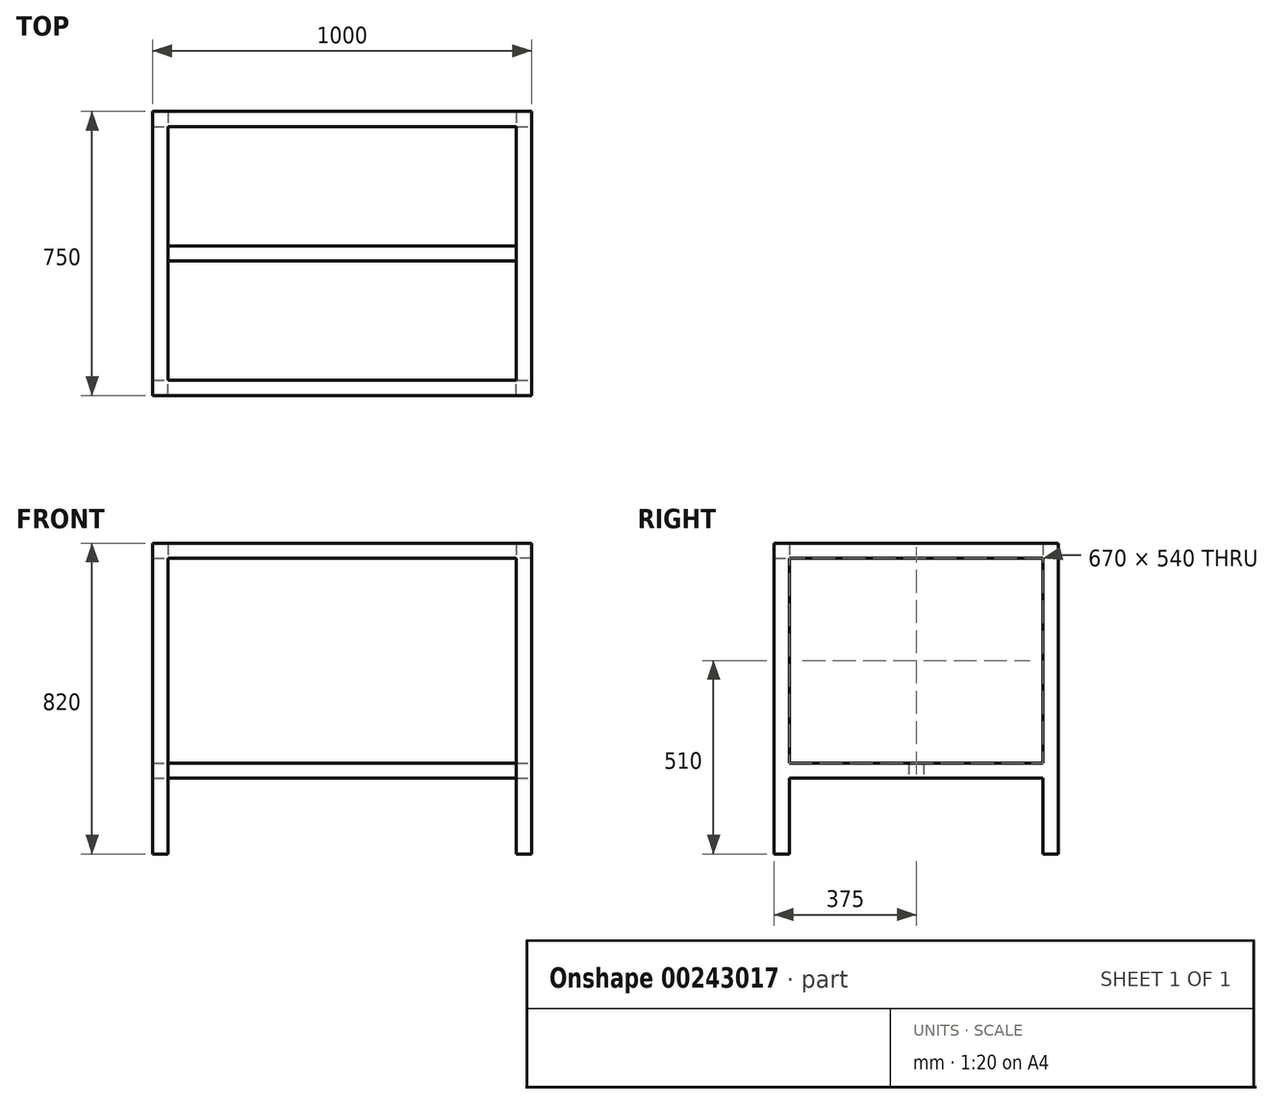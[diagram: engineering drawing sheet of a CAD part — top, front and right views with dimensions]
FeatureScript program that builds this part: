
annotation { "Feature Type Name" : "Feature", "Feature Type Description" : "" }
export const myFeature = defineFeature(function(context is Context, id is Id, definition is map)
    precondition{}
    {
        {
            var Q0;
            Q0=qCreatedBy(makeId("Top.planeOp"),FACE);
            var sketch = newSketch(context, id + "F0", { "sketchPlane" : qUnion([Q0])});
            skLineSegment(sketch, "E0.bottom", {"start": v(500, 375) * mm, "end": v(-500, 375) * mm});
            skLineSegment(sketch, "E0.top", {"start": v(500, -375) * mm, "end": v(-500, -375) * mm});
            skLineSegment(sketch, "E0.left", {"start": v(500, 375) * mm, "end": v(500, -375) * mm});
            skLineSegment(sketch, "E0.right", {"start": v(-500, 375) * mm, "end": v(-500, -375) * mm});
            skPoint(sketch, "E0.middle", {"position": v(0, 0) * mm});
            skLineSegment(sketch, "E1.bottom", {"start": v(460, 335) * mm, "end": v(0, 335) * mm});
            skLineSegment(sketch, "E1.top", {"start": v(460, -335) * mm, "end": v(0, -335) * mm});
            skLineSegment(sketch, "E1.left", {"start": v(460, 335) * mm, "end": v(460, -335) * mm});
            skLineSegment(sketch, "E1.right", {"start": v(-460, 335) * mm, "end": v(-460, -335) * mm});
            skLineSegment(sketch, "E2.trimOffspring", {"start": v(0, 335) * mm, "end": v(-460, 335) * mm});
            skLineSegment(sketch, "E3.trimOffspring", {"start": v(0, -335) * mm, "end": v(-460, -335) * mm});
            skSolve(sketch);
        }
        {
            var Q0;
            Q0 = qSketchRegion(id + "F0", true);
            extrude(context, id + "F1", {"entities" : qUnion([Q0]), "depth" : 40 * mm});
        }
        {
            var Q0;
            Q0=makeQuery(id+"F1.opExtrude","CAP_FACE",FACE,{"disambiguationData":[OSD([sQuery(id+"F0.wireOp",EDGE,"E0.bottom"),sQuery(id+"F0.wireOp",EDGE,"E0.top"),sQuery(id+"F0.wireOp",EDGE,"E0.left"),sQuery(id+"F0.wireOp",EDGE,"E0.right"),sQuery(id+"F0.wireOp",EDGE,"E1.bottom"),sQuery(id+"F0.wireOp",EDGE,"E1.top"),sQuery(id+"F0.wireOp",EDGE,"E1.left"),sQuery(id+"F0.wireOp",EDGE,"E1.right"),sQuery(id+"F0.wireOp",EDGE,"AlbXzI7k-iaXt-A7OD-96uh-BcEF6WzRrO9d"),sQuery(id+"F0.wireOp",EDGE,"s61sFKu2-3wUQ-j9Oy-KIh7-d0yx8tar7ZfR"),sQuery(id+"F0.wireOp",EDGE,"E2.trimOffspring"),sQuery(id+"F0.wireOp",EDGE,"E3.trimOffspring")])],"isStart":true});
            var sketch = newSketch(context, id + "F2", { "sketchPlane" : qUnion([Q0])});
            skLineSegment(sketch, "E4.bottom", {"start": v(-500, -375) * mm, "end": v(-460, -375) * mm});
            skLineSegment(sketch, "E4.top", {"start": v(-500, -335) * mm, "end": v(-460, -335) * mm});
            skLineSegment(sketch, "E4.left", {"start": v(-500, -375) * mm, "end": v(-500, -335) * mm});
            skLineSegment(sketch, "E4.right", {"start": v(-460, -375) * mm, "end": v(-460, -335) * mm});
            skLineSegment(sketch, "E5.bottom", {"start": v(-500, 375) * mm, "end": v(-460, 375) * mm});
            skLineSegment(sketch, "E5.top", {"start": v(-500, 335) * mm, "end": v(-460, 335) * mm});
            skLineSegment(sketch, "E5.left", {"start": v(-500, 375) * mm, "end": v(-500, 335) * mm});
            skLineSegment(sketch, "E5.right", {"start": v(-460, 375) * mm, "end": v(-460, 335) * mm});
            skLineSegment(sketch, "E6.bottom", {"start": v(500, 375) * mm, "end": v(460, 375) * mm});
            skLineSegment(sketch, "E6.top", {"start": v(500, 335) * mm, "end": v(460, 335) * mm});
            skLineSegment(sketch, "E6.left", {"start": v(500, 375) * mm, "end": v(500, 335) * mm});
            skLineSegment(sketch, "E6.right", {"start": v(460, 375) * mm, "end": v(460, 335) * mm});
            skLineSegment(sketch, "E7.bottom", {"start": v(500, -375) * mm, "end": v(460, -375) * mm});
            skLineSegment(sketch, "E7.top", {"start": v(500, -335) * mm, "end": v(460, -335) * mm});
            skLineSegment(sketch, "E7.left", {"start": v(500, -375) * mm, "end": v(500, -335) * mm});
            skLineSegment(sketch, "E7.right", {"start": v(460, -375) * mm, "end": v(460, -335) * mm});
            skSolve(sketch);
        }
        {
            var Q0;
            Q0 = qSketchRegion(id + "F2", true);
            extrude(context, id + "F3", {"entities" : qUnion([Q0]), "operationType" : NewBodyOperationType.ADD, "depth" : (820 - 40) * mm});
        }
        {
            var Q0;
            Q0=makeQuery(id+"F3.opExtrude","SWEPT_FACE",FACE,{"disambiguationData":[OSD([sQuery(id+"F2.wireOp",EDGE,"E4.top")])]});
            var sketch = newSketch(context, id + "F4", { "sketchPlane" : qUnion([Q0])});
            skLineSegment(sketch, "E8.bottom", {"start": v(-500, -540) * mm, "end": v(-460, -540) * mm});
            skLineSegment(sketch, "E8.top", {"start": v(-500, -580) * mm, "end": v(-460, -580) * mm});
            skLineSegment(sketch, "E8.left", {"start": v(-500, -540) * mm, "end": v(-500, -580) * mm});
            skLineSegment(sketch, "E8.right", {"start": v(-460, -540) * mm, "end": v(-460, -580) * mm});
            skSolve(sketch);
        }
        {
            var Q0;
            Q0 = qSketchRegion(id + "F4", true);
            extrude(context, id + "F5", {"entities" : qUnion([Q0]), "operationType" : NewBodyOperationType.ADD, "depth" : (750 - 80) * mm});
        }
        {
            var Q0;
            Q0=makeQuery(id+"F3.opExtrude","SWEPT_FACE",FACE,{"disambiguationData":[OSD([sQuery(id+"F2.wireOp",EDGE,"E7.top")])]});
            var sketch = newSketch(context, id + "F6", { "sketchPlane" : qUnion([Q0])});
            skLineSegment(sketch, "E9.bottom", {"start": v(460, -540) * mm, "end": v(500, -540) * mm});
            skLineSegment(sketch, "E9.top", {"start": v(460, -580) * mm, "end": v(500, -580) * mm});
            skLineSegment(sketch, "E9.left", {"start": v(460, -540) * mm, "end": v(460, -580) * mm});
            skLineSegment(sketch, "E9.right", {"start": v(500, -540) * mm, "end": v(500, -580) * mm});
            skSolve(sketch);
        }
        {
            var Q0;
            Q0 = qSketchRegion(id + "F6", true);
            extrude(context, id + "F7", {"entities" : qUnion([Q0]), "operationType" : NewBodyOperationType.ADD, "depth" : (750 - 80) * mm});
        }
        {
            var Q0;
            Q0=makeQuery(id+"F7.boolean.opBoolean","MERGE",FACE,{"derivedFrom":[makeQuery(id+"F3.opExtrude","SWEPT_FACE",FACE,{"disambiguationData":[OSD([sQuery(id+"F2.wireOp",EDGE,"E6.right")])]}),makeQuery(id+"F3.opExtrude","SWEPT_FACE",FACE,{"disambiguationData":[OSD([sQuery(id+"F2.wireOp",EDGE,"E7.right")])]}),makeQuery(id+"F7.opExtrude","SWEPT_FACE",FACE,{"disambiguationData":[OSD([sQuery(id+"F6.wireOp",EDGE,"E9.left")])]})]});
            var sketch = newSketch(context, id + "F8", { "sketchPlane" : qUnion([Q0])});
            skLineSegment(sketch, "E10.bottom", {"start": v(20, -540) * mm, "end": v(-20, -540) * mm});
            skLineSegment(sketch, "E10.top", {"start": v(20, -580) * mm, "end": v(-20, -580) * mm});
            skLineSegment(sketch, "E10.left", {"start": v(20, -540) * mm, "end": v(20, -580) * mm});
            skLineSegment(sketch, "E10.right", {"start": v(-20, -540) * mm, "end": v(-20, -580) * mm});
            skPoint(sketch, "E10.middle", {"position": v(0, -560) * mm});
            skPoint(sketch, "E10.middle.positionSnap0", {"position": v(0, -540) * mm});
            skPoint(sketch, "E10.centerSnap0", {"position": v(0, -540) * mm});
            skSolve(sketch);
        }
        {
            var Q0;
            Q0 = qSketchRegion(id + "F8", true);
            extrude(context, id + "F9", {"entities" : qUnion([Q0]), "operationType" : NewBodyOperationType.ADD, "depth" : (1000 - 80) * mm});
        }
    });
